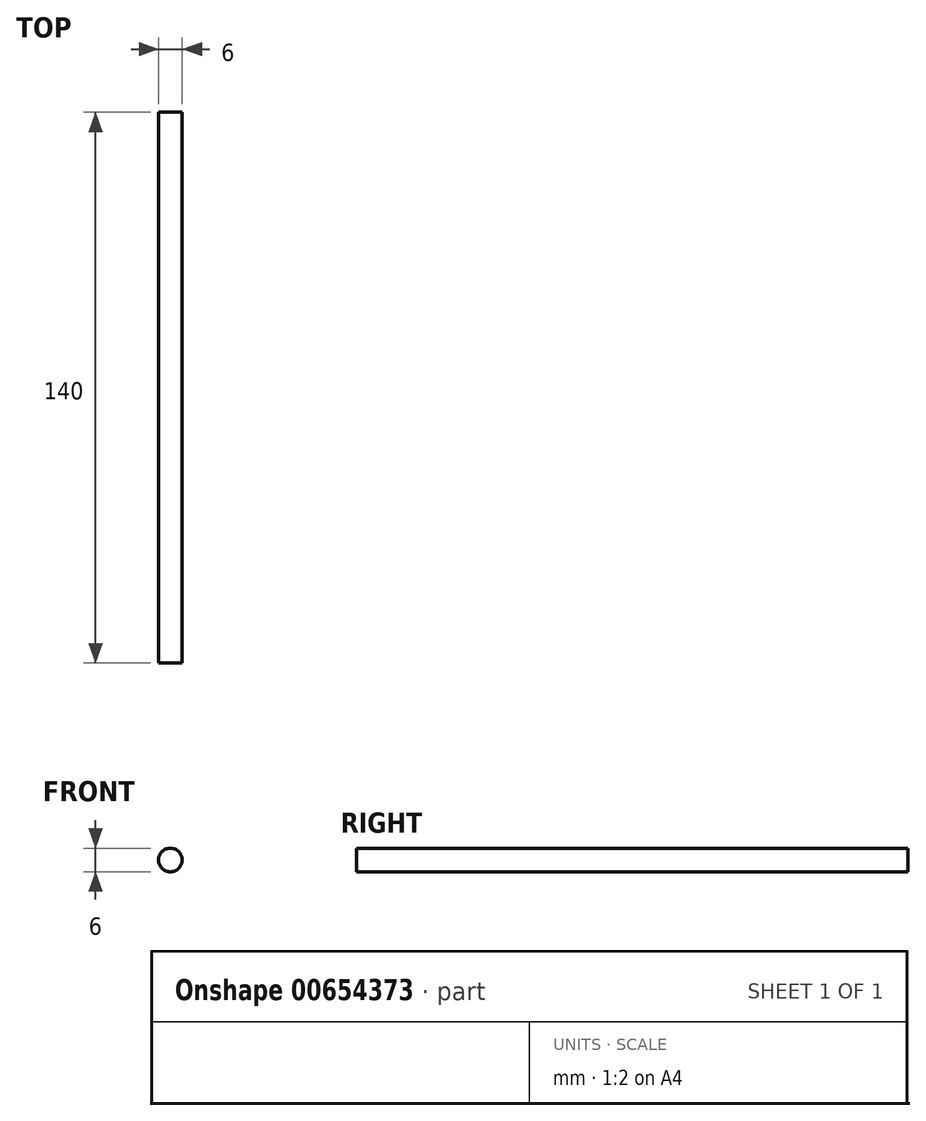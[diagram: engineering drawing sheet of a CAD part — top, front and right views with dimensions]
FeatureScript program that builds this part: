
annotation { "Feature Type Name" : "Feature", "Feature Type Description" : "" }
export const myFeature = defineFeature(function(context is Context, id is Id, definition is map)
    precondition{}
    {
        {
            assignVariable(context, id + "F0", {"name" : "lunghezza", "anyValue" : 140 * mm});
        }
        {
            var Q0;
            Q0=qCreatedBy(makeId("Front.planeOp"),FACE);
            var sketch = newSketch(context, id + "F1", { "sketchPlane" : qUnion([Q0])});
            skCircle(sketch, "E0", {"center": v(0, 0) * mm, "radius": 3 * mm});
            skSolve(sketch);
        }
        {
            var Q0;
            Q0=makeQuery(id+"F1.imprint","IMPRINT",FACE,{"disambiguationData":[TD([[makeQuery(id+"F1.imprint","IMPRINT",EDGE,{"derivedFrom":sQuery(id+"F1.wireOp",EDGE,"E0")}),1.0]])]});
            extrude(context, id + "F2", {"entities" : qUnion([Q0]), "depth" : getVariable(context, 'lunghezza'), "offsetDistance" : 25 * mm});
        }
    });
